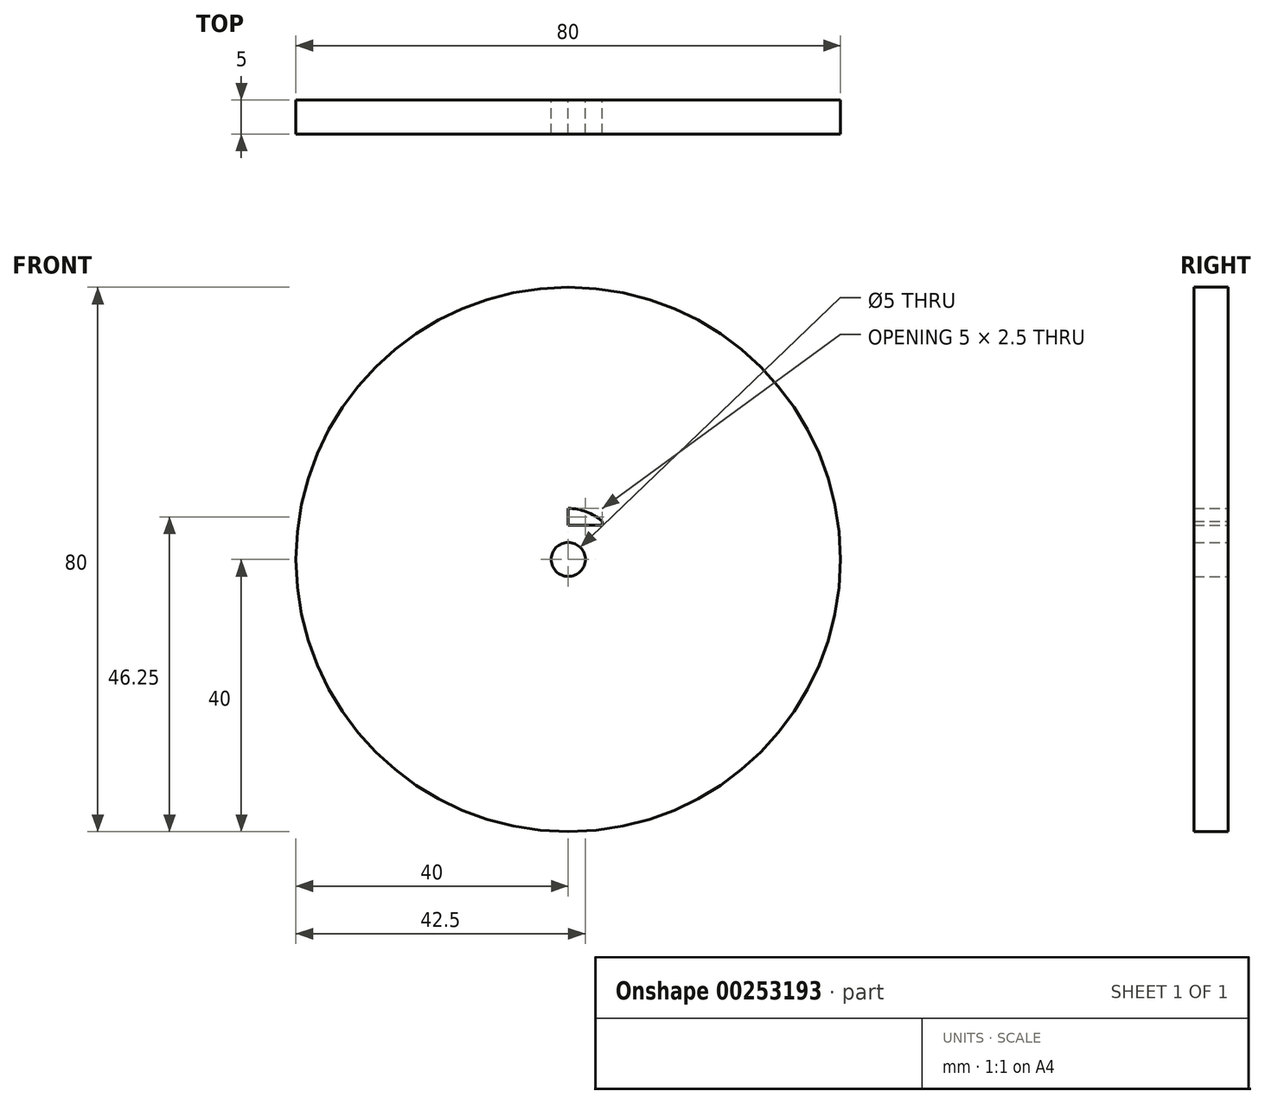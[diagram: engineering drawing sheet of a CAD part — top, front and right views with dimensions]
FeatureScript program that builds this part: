
annotation { "Feature Type Name" : "Feature", "Feature Type Description" : "" }
export const myFeature = defineFeature(function(context is Context, id is Id, definition is map)
    precondition{}
    {
        {
            var Q0;
            Q0=qCreatedBy(makeId("Front.planeOp"),FACE);
            var sketch = newSketch(context, id + "F0", { "sketchPlane" : qUnion([Q0])});
            skCircle(sketch, "E0", {"center": v(0, 0) * mm, "radius": 40 * mm});
            skCircle(sketch, "E1", {"center": v(0, 0) * mm, "radius": 31 * mm});
            skCircle(sketch, "E2", {"center": v(0, 0) * mm, "radius": 7.5 * mm});
            skCircle(sketch, "E3", {"center": v(0, 0) * mm, "radius": 2.5 * mm});
            skLineSegment(sketch, "E4", {"start": v(0, 0) * mm, "end": v(0, 40) * mm});
            skLineSegment(sketch, "E5", {"start": v(0, 0) * mm, "end": v(40, 0) * mm});
            skLineSegment(sketch, "E6", {"start": v(0, 0) * mm, "end": v(0, -40) * mm});
            skLineSegment(sketch, "E7", {"start": v(0, 0) * mm, "end": v(-40, 0) * mm});
            skLineSegment(sketch, "E8.0", {"start": v(5, 0) * mm, "end": v(5, 40) * mm});
            skLineSegment(sketch, "E9.0", {"start": v(-5, 0) * mm, "end": v(-5, 40) * mm});
            skLineSegment(sketch, "E10.0", {"start": v(0, -5) * mm, "end": v(40, -5) * mm});
            skLineSegment(sketch, "E11.0", {"start": v(0, 5) * mm, "end": v(40, 5) * mm});
            skLineSegment(sketch, "E12.0", {"start": v(-5, 0) * mm, "end": v(-5, -40) * mm});
            skLineSegment(sketch, "E13.0", {"start": v(5, 0) * mm, "end": v(5, -40) * mm});
            skLineSegment(sketch, "E14.0", {"start": v(0, 5) * mm, "end": v(-40, 5) * mm});
            skLineSegment(sketch, "E15.0", {"start": v(0, -5) * mm, "end": v(-40, -5) * mm});
            skSolve(sketch);
        }
        {
            var Q0;
            Q0 = qSketchRegion(id + "F0", true);
            var Q1;
            {var subQ0=sQuery(id+"F0.wireOp",EDGE,"E8.0");var subQ1=sQuery(id+"F0.wireOp",EDGE,"E1");var subQ2=makeQuery(id+"F0.imprint","INTERSECT",VERTEX,{"derivedFrom":[subQ1,subQ0]});Q1=makeQuery(id+"F0.imprint","IMPRINT",FACE,{"disambiguationData":[TD([[makeQuery(id+"F0.imprint","IMPRINT",EDGE,{"disambiguationData":[TD([[subQ2,-1.0]])],"derivedFrom":subQ1}),1.0]])]});}
            var Q2;
            {var subQ0=sQuery(id+"F0.wireOp",EDGE,"E4");var subQ1=sQuery(id+"F0.wireOp",EDGE,"E1");var subQ2=makeQuery(id+"F0.imprint","INTERSECT",VERTEX,{"derivedFrom":[subQ1,subQ0]});Q2=makeQuery(id+"F0.imprint","IMPRINT",FACE,{"disambiguationData":[TD([[makeQuery(id+"F0.imprint","IMPRINT",EDGE,{"disambiguationData":[TD([[subQ2,-1.0]])],"derivedFrom":subQ1}),1.0]])]});}
            var Q3;
            {var subQ0=sQuery(id+"F0.wireOp",EDGE,"E14.0");var subQ1=sQuery(id+"F0.wireOp",EDGE,"E1");var subQ2=makeQuery(id+"F0.imprint","INTERSECT",VERTEX,{"derivedFrom":[subQ1,subQ0]});Q3=makeQuery(id+"F0.imprint","IMPRINT",FACE,{"disambiguationData":[TD([[makeQuery(id+"F0.imprint","IMPRINT",EDGE,{"disambiguationData":[TD([[subQ2,-1.0]])],"derivedFrom":subQ1}),1.0]])]});}
            var Q4;
            {var subQ0=sQuery(id+"F0.wireOp",EDGE,"E7");var subQ1=sQuery(id+"F0.wireOp",EDGE,"E1");var subQ2=makeQuery(id+"F0.imprint","INTERSECT",VERTEX,{"derivedFrom":[subQ1,subQ0]});Q4=makeQuery(id+"F0.imprint","IMPRINT",FACE,{"disambiguationData":[TD([[makeQuery(id+"F0.imprint","IMPRINT",EDGE,{"disambiguationData":[TD([[subQ2,-1.0]])],"derivedFrom":subQ1}),1.0]])]});}
            var Q5;
            {var subQ0=sQuery(id+"F0.wireOp",EDGE,"E12.0");var subQ1=sQuery(id+"F0.wireOp",EDGE,"E1");var subQ2=makeQuery(id+"F0.imprint","INTERSECT",VERTEX,{"derivedFrom":[subQ1,subQ0]});Q5=makeQuery(id+"F0.imprint","IMPRINT",FACE,{"disambiguationData":[TD([[makeQuery(id+"F0.imprint","IMPRINT",EDGE,{"disambiguationData":[TD([[subQ2,-1.0]])],"derivedFrom":subQ1}),1.0]])]});}
            var Q6;
            {var subQ0=sQuery(id+"F0.wireOp",EDGE,"E6");var subQ1=sQuery(id+"F0.wireOp",EDGE,"E1");var subQ2=makeQuery(id+"F0.imprint","INTERSECT",VERTEX,{"derivedFrom":[subQ1,subQ0]});Q6=makeQuery(id+"F0.imprint","IMPRINT",FACE,{"disambiguationData":[TD([[makeQuery(id+"F0.imprint","IMPRINT",EDGE,{"disambiguationData":[TD([[subQ2,-1.0]])],"derivedFrom":subQ1}),1.0]])]});}
            var Q7;
            {var subQ0=sQuery(id+"F0.wireOp",EDGE,"E5");var subQ1=sQuery(id+"F0.wireOp",EDGE,"E1");var subQ2=makeQuery(id+"F0.imprint","INTERSECT",VERTEX,{"derivedFrom":[subQ1,subQ0]});Q7=makeQuery(id+"F0.imprint","IMPRINT",FACE,{"disambiguationData":[TD([[makeQuery(id+"F0.imprint","IMPRINT",EDGE,{"disambiguationData":[TD([[subQ2,1.0]])],"derivedFrom":subQ1}),1.0]])]});}
            var Q8;
            {var subQ0=sQuery(id+"F0.wireOp",EDGE,"E11.0");var subQ1=sQuery(id+"F0.wireOp",EDGE,"E1");var subQ2=makeQuery(id+"F0.imprint","INTERSECT",VERTEX,{"derivedFrom":[subQ1,subQ0]});Q8=makeQuery(id+"F0.imprint","IMPRINT",FACE,{"disambiguationData":[TD([[makeQuery(id+"F0.imprint","IMPRINT",EDGE,{"disambiguationData":[TD([[subQ2,1.0]])],"derivedFrom":subQ1}),1.0]])]});}
            var Q9;
            {var subQ0=sQuery(id+"F0.wireOp",EDGE,"E11.0");var subQ1=sQuery(id+"F0.wireOp",EDGE,"E2");var subQ2=makeQuery(id+"F0.imprint","INTERSECT",VERTEX,{"derivedFrom":[subQ1,subQ0]});Q9=makeQuery(id+"F0.imprint","IMPRINT",FACE,{"disambiguationData":[TD([[makeQuery(id+"F0.imprint","IMPRINT",EDGE,{"disambiguationData":[TD([[subQ2,1.0]])],"derivedFrom":subQ1}),1.0]])]});}
            var Q10;
            {var subQ5=sQuery(id+"F0.wireOp",EDGE,"E3");var subQ7=sQuery(id+"F0.wireOp",EDGE,"E4");var subQ9=makeQuery(id+"F0.imprint","INTERSECT",VERTEX,{"derivedFrom":[subQ5,subQ7]});Q10=makeQuery(id+"F0.imprint","IMPRINT",FACE,{"disambiguationData":[TD([[makeQuery(id+"F0.imprint","IMPRINT",EDGE,{"disambiguationData":[TD([[subQ9,1.0]])],"derivedFrom":subQ5}),-1.0]])]});}
            var Q11;
            {var subQ0=sQuery(id+"F0.wireOp",EDGE,"E8.0");var subQ1=sQuery(id+"F0.wireOp",EDGE,"E2");var subQ2=makeQuery(id+"F0.imprint","INTERSECT",VERTEX,{"derivedFrom":[subQ1,subQ0]});Q11=makeQuery(id+"F0.imprint","IMPRINT",FACE,{"disambiguationData":[TD([[makeQuery(id+"F0.imprint","IMPRINT",EDGE,{"disambiguationData":[TD([[subQ2,-1.0]])],"derivedFrom":subQ1}),1.0]])]});}
            var Q12;
            {var subQ0=sQuery(id+"F0.wireOp",EDGE,"E4");var subQ1=sQuery(id+"F0.wireOp",EDGE,"E2");var subQ2=makeQuery(id+"F0.imprint","INTERSECT",VERTEX,{"derivedFrom":[subQ1,subQ0]});Q12=makeQuery(id+"F0.imprint","IMPRINT",FACE,{"disambiguationData":[TD([[makeQuery(id+"F0.imprint","IMPRINT",EDGE,{"disambiguationData":[TD([[subQ2,-1.0]])],"derivedFrom":subQ1}),1.0]])]});}
            var Q13;
            {var subQ3=sQuery(id+"F0.wireOp",EDGE,"E3");var subQ6=sQuery(id+"F0.wireOp",EDGE,"E4");var subQ8=makeQuery(id+"F0.imprint","INTERSECT",VERTEX,{"derivedFrom":[subQ3,subQ6]});Q13=makeQuery(id+"F0.imprint","IMPRINT",FACE,{"disambiguationData":[TD([[makeQuery(id+"F0.imprint","IMPRINT",EDGE,{"disambiguationData":[TD([[subQ8,-1.0]])],"derivedFrom":subQ3}),-1.0]])]});}
            var Q14;
            {var subQ0=sQuery(id+"F0.wireOp",EDGE,"E14.0");var subQ1=sQuery(id+"F0.wireOp",EDGE,"E2");var subQ2=makeQuery(id+"F0.imprint","INTERSECT",VERTEX,{"derivedFrom":[subQ1,subQ0]});Q14=makeQuery(id+"F0.imprint","IMPRINT",FACE,{"disambiguationData":[TD([[makeQuery(id+"F0.imprint","IMPRINT",EDGE,{"disambiguationData":[TD([[subQ2,-1.0]])],"derivedFrom":subQ1}),1.0]])]});}
            var Q15;
            {var subQ0=sQuery(id+"F0.wireOp",EDGE,"E7");var subQ1=sQuery(id+"F0.wireOp",EDGE,"E2");var subQ2=makeQuery(id+"F0.imprint","INTERSECT",VERTEX,{"derivedFrom":[subQ1,subQ0]});Q15=makeQuery(id+"F0.imprint","IMPRINT",FACE,{"disambiguationData":[TD([[makeQuery(id+"F0.imprint","IMPRINT",EDGE,{"disambiguationData":[TD([[subQ2,-1.0]])],"derivedFrom":subQ1}),1.0]])]});}
            var Q16;
            {var subQ1=sQuery(id+"F0.wireOp",EDGE,"E7");var subQ7=sQuery(id+"F0.wireOp",EDGE,"E3");var subQ9=makeQuery(id+"F0.imprint","INTERSECT",VERTEX,{"derivedFrom":[subQ7,subQ1]});Q16=makeQuery(id+"F0.imprint","IMPRINT",FACE,{"disambiguationData":[TD([[makeQuery(id+"F0.imprint","IMPRINT",EDGE,{"disambiguationData":[TD([[subQ9,-1.0]])],"derivedFrom":subQ7}),-1.0]])]});}
            var Q17;
            {var subQ3=sQuery(id+"F0.wireOp",EDGE,"E3");var subQ6=sQuery(id+"F0.wireOp",EDGE,"E5");var subQ8=makeQuery(id+"F0.imprint","INTERSECT",VERTEX,{"derivedFrom":[subQ3,subQ6]});Q17=makeQuery(id+"F0.imprint","IMPRINT",FACE,{"disambiguationData":[TD([[makeQuery(id+"F0.imprint","IMPRINT",EDGE,{"disambiguationData":[TD([[subQ8,1.0]])],"derivedFrom":subQ3}),-1.0]])]});}
            var Q18;
            {var subQ0=sQuery(id+"F0.wireOp",EDGE,"E5");var subQ1=sQuery(id+"F0.wireOp",EDGE,"E2");var subQ2=makeQuery(id+"F0.imprint","INTERSECT",VERTEX,{"derivedFrom":[subQ1,subQ0]});Q18=makeQuery(id+"F0.imprint","IMPRINT",FACE,{"disambiguationData":[TD([[makeQuery(id+"F0.imprint","IMPRINT",EDGE,{"disambiguationData":[TD([[subQ2,1.0]])],"derivedFrom":subQ1}),1.0]])]});}
            var Q19;
            {var subQ0=sQuery(id+"F0.wireOp",EDGE,"E6");var subQ1=sQuery(id+"F0.wireOp",EDGE,"E2");var subQ2=makeQuery(id+"F0.imprint","INTERSECT",VERTEX,{"derivedFrom":[subQ1,subQ0]});Q19=makeQuery(id+"F0.imprint","IMPRINT",FACE,{"disambiguationData":[TD([[makeQuery(id+"F0.imprint","IMPRINT",EDGE,{"disambiguationData":[TD([[subQ2,-1.0]])],"derivedFrom":subQ1}),1.0]])]});}
            var Q20;
            {var subQ0=sQuery(id+"F0.wireOp",EDGE,"E9.0");var subQ1=sQuery(id+"F0.wireOp",EDGE,"E2");var subQ2=makeQuery(id+"F0.imprint","INTERSECT",VERTEX,{"derivedFrom":[subQ1,subQ0]});Q20=makeQuery(id+"F0.imprint","IMPRINT",FACE,{"disambiguationData":[TD([[makeQuery(id+"F0.imprint","IMPRINT",EDGE,{"disambiguationData":[TD([[subQ2,-1.0]])],"derivedFrom":subQ1}),1.0]])]});}
            var Q21;
            {var subQ0=sQuery(id+"F0.wireOp",EDGE,"E15.0");var subQ1=sQuery(id+"F0.wireOp",EDGE,"E2");var subQ2=makeQuery(id+"F0.imprint","INTERSECT",VERTEX,{"derivedFrom":[subQ1,subQ0]});Q21=makeQuery(id+"F0.imprint","IMPRINT",FACE,{"disambiguationData":[TD([[makeQuery(id+"F0.imprint","IMPRINT",EDGE,{"disambiguationData":[TD([[subQ2,-1.0]])],"derivedFrom":subQ1}),1.0]])]});}
            var Q22;
            {var subQ0=sQuery(id+"F0.wireOp",EDGE,"E12.0");var subQ1=sQuery(id+"F0.wireOp",EDGE,"E2");var subQ2=makeQuery(id+"F0.imprint","INTERSECT",VERTEX,{"derivedFrom":[subQ1,subQ0]});Q22=makeQuery(id+"F0.imprint","IMPRINT",FACE,{"disambiguationData":[TD([[makeQuery(id+"F0.imprint","IMPRINT",EDGE,{"disambiguationData":[TD([[subQ2,-1.0]])],"derivedFrom":subQ1}),1.0]])]});}
            var Q23;
            {var subQ0=sQuery(id+"F0.wireOp",EDGE,"E13.0");var subQ1=sQuery(id+"F0.wireOp",EDGE,"E2");var subQ2=makeQuery(id+"F0.imprint","INTERSECT",VERTEX,{"derivedFrom":[subQ1,subQ0]});Q23=makeQuery(id+"F0.imprint","IMPRINT",FACE,{"disambiguationData":[TD([[makeQuery(id+"F0.imprint","IMPRINT",EDGE,{"disambiguationData":[TD([[subQ2,-1.0]])],"derivedFrom":subQ1}),1.0]])]});}
            var Q24;
            {var subQ0=sQuery(id+"F0.wireOp",EDGE,"E11.0");var subQ1=sQuery(id+"F0.wireOp",EDGE,"E2");var subQ2=makeQuery(id+"F0.imprint","INTERSECT",VERTEX,{"derivedFrom":[subQ1,subQ0]});Q24=makeQuery(id+"F0.imprint","IMPRINT",FACE,{"disambiguationData":[TD([[makeQuery(id+"F0.imprint","IMPRINT",EDGE,{"disambiguationData":[TD([[subQ2,-1.0]])],"derivedFrom":subQ1}),1.0]])]});}
            extrude(context, id + "F1", {"entities" : qUnion([Q0, Q1, Q2, Q3, Q4, Q5, Q6, Q7, Q8, Q9, Q10, Q11, Q12, Q13, Q14, Q15, Q16, Q17, Q18, Q19, Q20, Q21, Q22, Q23, Q24]), "endBound" : BoundingType.SYMMETRIC, "depth" : 5 * mm});
        }
    });
